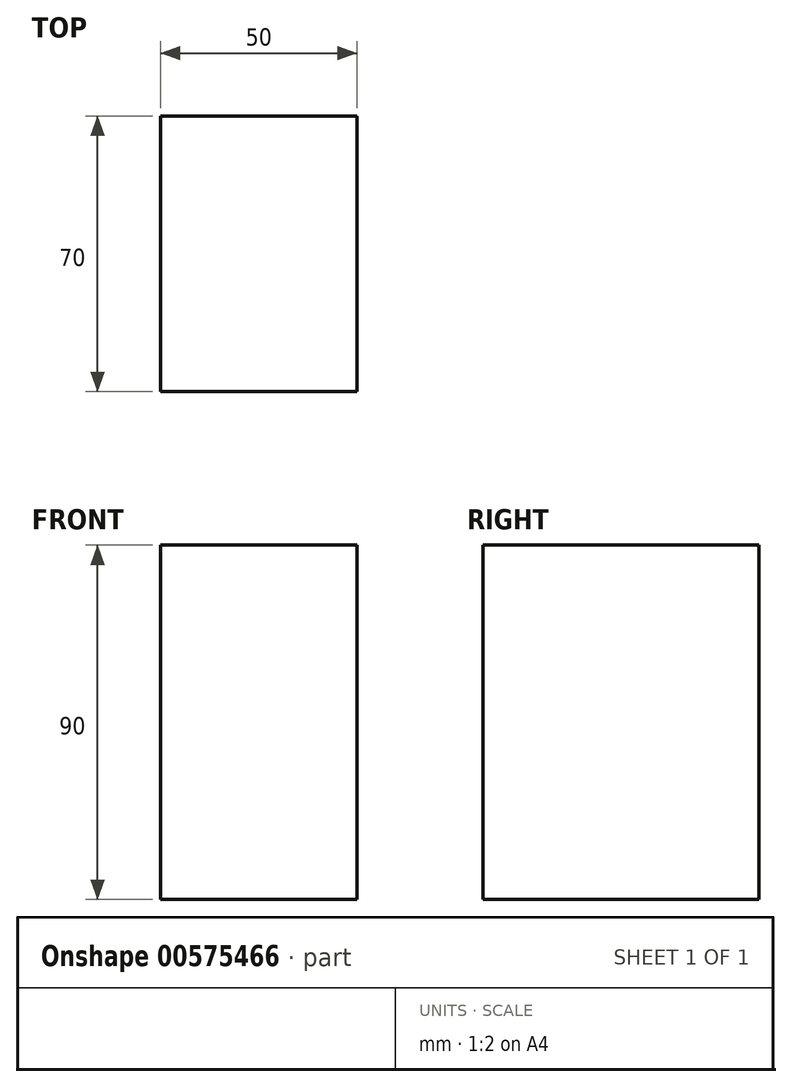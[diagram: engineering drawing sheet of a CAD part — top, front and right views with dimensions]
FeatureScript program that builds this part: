
annotation { "Feature Type Name" : "Feature", "Feature Type Description" : "" }
export const myFeature = defineFeature(function(context is Context, id is Id, definition is map)
    precondition{}
    {
        {
            var Q0;
            Q0=qCreatedBy(makeId("Top.planeOp"),FACE);
            var sketch = newSketch(context, id + "F0", { "sketchPlane" : qUnion([Q0])});
            skLineSegment(sketch, "E0.bottom", {"start": v(0, 0) * mm, "end": v(50, 0) * mm});
            skLineSegment(sketch, "E0.top", {"start": v(0, 70) * mm, "end": v(50, 70) * mm});
            skLineSegment(sketch, "E0.left", {"start": v(0, 0) * mm, "end": v(0, 70) * mm});
            skLineSegment(sketch, "E0.right", {"start": v(50, 0) * mm, "end": v(50, 70) * mm});
            skSolve(sketch);
        }
        {
            var Q0;
            Q0=makeQuery(id+"F0.imprint","IMPRINT",FACE,{"disambiguationData":[TD([[makeQuery(id+"F0.imprint","IMPRINT",EDGE,{"derivedFrom":sQuery(id+"F0.wireOp",EDGE,"E0.bottom")}),1.0]])]});
            extrude(context, id + "F1", {"entities" : qUnion([Q0]), "depth" : 90 * mm, "offsetDistance" : 25 * mm});
        }
    });
